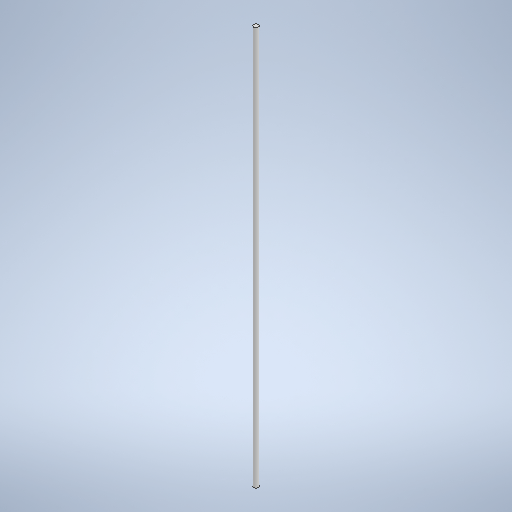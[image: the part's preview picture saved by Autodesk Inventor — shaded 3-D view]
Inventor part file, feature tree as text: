
AUTODESK INVENTOR PART (.ipt)
format: ipt  version: 2025.1 (Build 291241000, 241)  size: 231,424 bytes
history: native  units: mm
features: extrude x1, sketch x1
ambient origin geometry x8: Origin, YZ Plane, XZ Plane, XY Plane, X Axis, Y Axis, Z Axis, Center Point
bodies: Solide1 (feature_tree)
feature tree (2):
  extrude  "Extrusion1"  Depth=3.0mm
  sketch  "Esquisse1"
